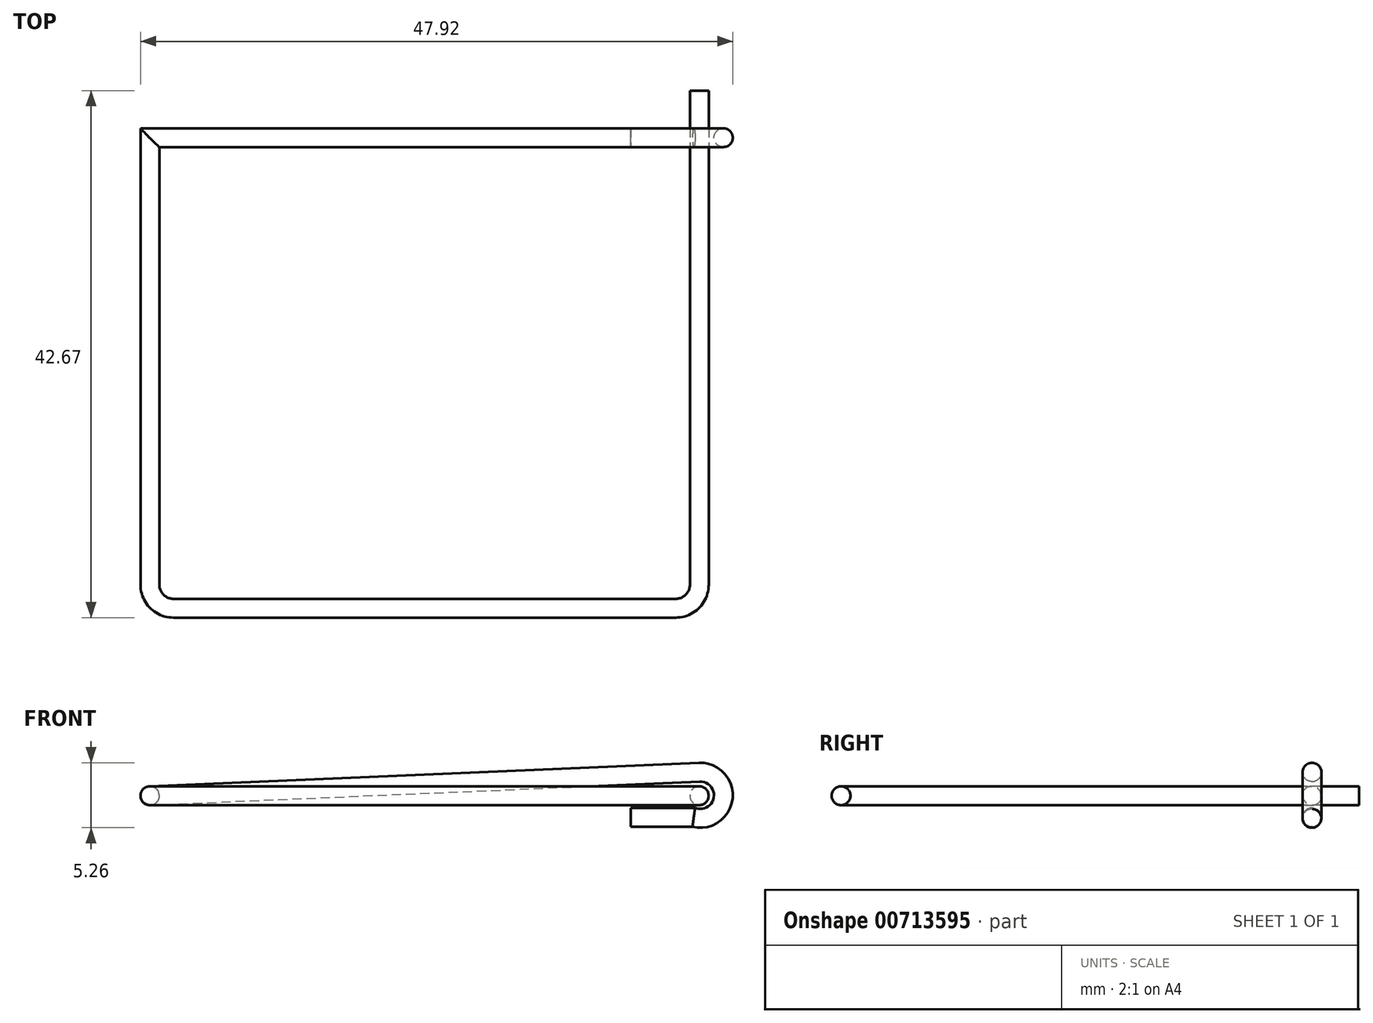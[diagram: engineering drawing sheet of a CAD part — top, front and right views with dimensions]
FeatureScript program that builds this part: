
annotation { "Feature Type Name" : "Feature", "Feature Type Description" : "" }
export const myFeature = defineFeature(function(context is Context, id is Id, definition is map)
    precondition{}
    {
        {
            var Q0;
            Q0=qCreatedBy(makeId("Top.planeOp"),FACE);
            var sketch = newSketch(context, id + "F0", { "sketchPlane" : qUnion([Q0])});
            skLineSegment(sketch, "E0", {"start": v(44.45, 3.81) * mm, "end": v(44.45, -36.2) * mm});
            skLineSegment(sketch, "E1", {"start": v(42.55, -38.1) * mm, "end": v(1.9, -38.1) * mm});
            skLineSegment(sketch, "E2", {"start": v(0, -36.2) * mm, "end": v(0, 0) * mm});
            skPoint(sketch, "E3.visualSharp", {"position": v(44.45, -38.1) * mm});
            skArc(sketch, "E3.filletArc", {"start": v(42.55, -38.1) * mm, "mid": v(43.9, -37.54) * mm, "end": v(44.45, -36.2) * mm});
            skPoint(sketch, "E4.visualSharp", {"position": v(0, -38.1) * mm});
            skArc(sketch, "E4.filletArc", {"start": v(0, -36.2) * mm, "mid": v(0.56, -37.54) * mm, "end": v(1.9, -38.1) * mm});
            skSolve(sketch);
        }
        {
            var Q0;
            Q0=qCreatedBy(makeId("Front.planeOp"),FACE);
            var sketch = newSketch(context, id + "F1", { "sketchPlane" : qUnion([Q0])});
            skLineSegment(sketch, "E5", {"start": v(44.45, 0) * mm, "end": v(44.45, 1.9) * mm});
            skLineSegment(sketch, "E6", {"start": v(0, 0) * mm, "end": v(44.45, 1.9) * mm});
            skArc(sketch, "E7", {"start": v(44.45, 1.9) * mm, "mid": v(46.38, -0.2) * mm, "end": v(44, -1.75) * mm});
            skLineSegment(sketch, "E8", {"start": v(44, -1.75) * mm, "end": v(38.92, -1.75) * mm});
            skCircle(sketch, "E9", {"center": v(44.45, 0) * mm, "radius": 0.76 * mm});
            skSolve(sketch);
        }
        {
            var Q0;
            Q0=sQuery(id+"F0.wireOp",VERTEX,"E4.filletArc.start");
            var Q1;
            Q1=sQuery(id+"F1.wireOp",VERTEX,"E6.start");
            var Q2;
            Q2=sQuery(id+"F1.wireOp",VERTEX,"E7.start");
            cPlane(context, id + "F2", {"entities" : qUnion([Q0, Q1, Q2]), "cplaneType" : CPlaneType.THREE_POINT, "offset" : 25.4 * mm, "width" : 152.4 * mm, "height" : 152.4 * mm});
        }
        {
            var Q0;
            Q0=makeQuery(id+"F1.imprint","IMPRINT",FACE,{"disambiguationData":[TD([[makeQuery(id+"F1.imprint","IMPRINT",EDGE,{"derivedFrom":sQuery(id+"F1.wireOp",EDGE,"E9")}),1.0]])]});
            var Q1;
            Q1=sQuery(id+"F0.wireOp",EDGE,"E0");
            var Q2;
            Q2=sQuery(id+"F0.wireOp",EDGE,"E3.filletArc");
            var Q3;
            Q3=sQuery(id+"F0.wireOp",EDGE,"E1");
            var Q4;
            Q4=sQuery(id+"F0.wireOp",EDGE,"E4.filletArc");
            var Q5;
            Q5=sQuery(id+"F0.wireOp",EDGE,"E2");
            var Q6;
            Q6=sQuery(id+"F1.wireOp",EDGE,"E6");
            var Q7;
            Q7=sQuery(id+"F1.wireOp",EDGE,"E7");
            var Q8;
            Q8=sQuery(id+"F1.wireOp",EDGE,"E8");
            sweep(context, id + "F3", {"profiles" : qUnion([Q0]), "path" : qUnion([Q1, Q2, Q3, Q4, Q5, Q6, Q7, Q8])});
        }
    });
